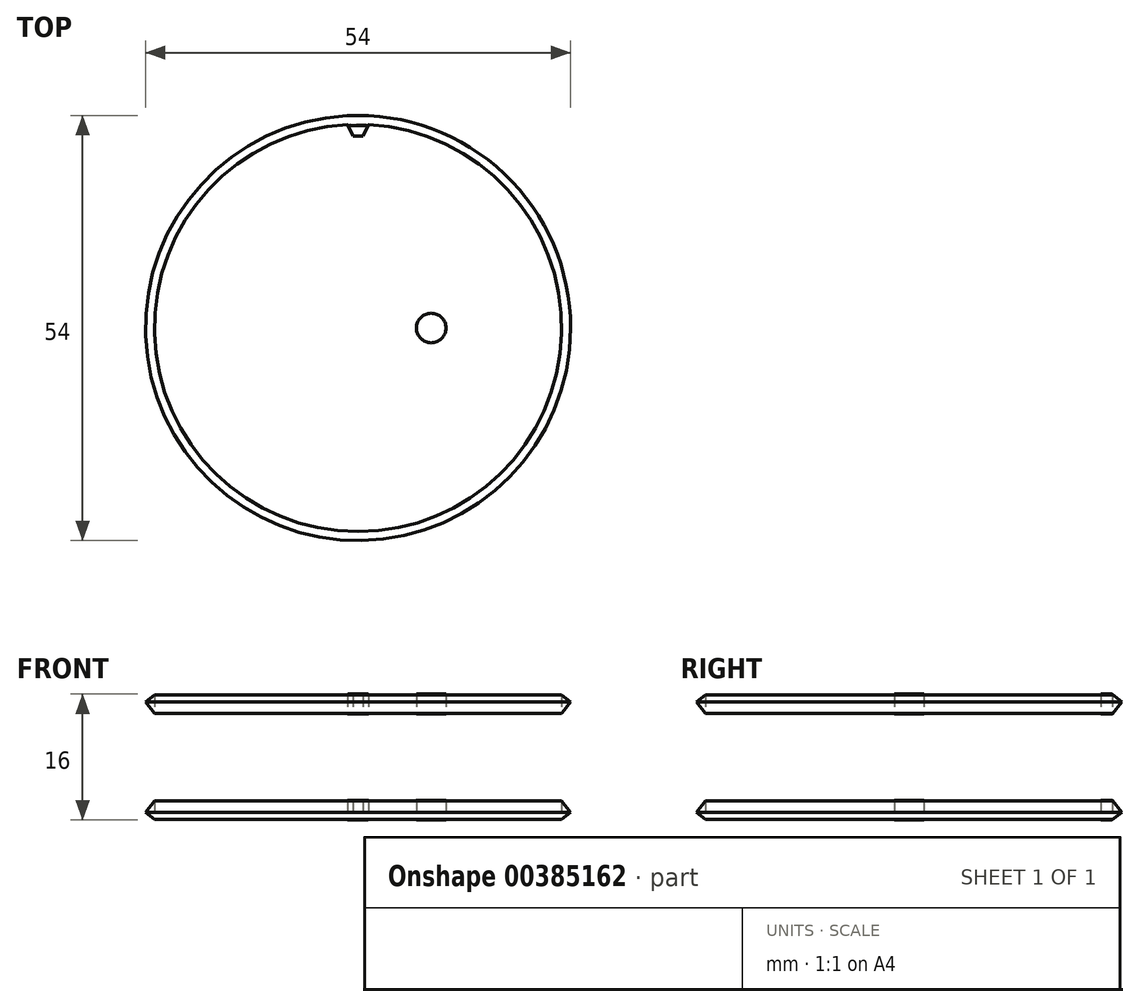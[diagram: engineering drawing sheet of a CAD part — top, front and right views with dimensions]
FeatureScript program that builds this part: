
annotation { "Feature Type Name" : "Feature", "Feature Type Description" : "" }
export const myFeature = defineFeature(function(context is Context, id is Id, definition is map)
    precondition{}
    {
        {
            var Q0;
            Q0=qCreatedBy(makeId("Top.planeOp"),FACE);
            var sketch = newSketch(context, id + "F0", { "sketchPlane" : qUnion([Q0])});
            skArc(sketch, "E0", {"start": v(-1.34, 25.84) * mm, "mid": v(0, -25.87) * mm, "end": v(1.34, 25.84) * mm});
            skCircle(sketch, "E1", {"center": v(0, 0) * mm, "radius": 24.37 * mm, "construction": true});
            skLineSegment(sketch, "E2", {"start": v(-0.65, 24.36) * mm, "end": v(-1.34, 25.84) * mm});
            skCircle(sketch, "E3", {"center": v(0, 0) * mm, "radius": 4.75 * mm});
            skArc(sketch, "E4", {"start": v(-0.65, 24.36) * mm, "mid": v(-0.33, 24.37) * mm, "end": v(0, 24.37) * mm});
            skLineSegment(sketch, "E5.MirrorCS", {"start": v(0.65, 24.36) * mm, "end": v(1.34, 25.84) * mm});
            skArc(sketch, "E6", {"start": v(-1.34, 25.84) * mm, "mid": v(0, 25.87) * mm, "end": v(1.34, 25.84) * mm});
            skArc(sketch, "E7.MirrorCS", {"start": v(0.65, 24.36) * mm, "mid": v(0.33, 24.37) * mm, "end": v(0, 24.37) * mm});
            skCircle(sketch, "E8", {"center": v(-9.3, 0) * mm, "radius": 1.88 * mm});
            skCircle(sketch, "E9.MirrorC", {"center": v(9.3, 0) * mm, "radius": 1.88 * mm});
            skSolve(sketch);
        }
        {
            var Q0;
            Q0=makeQuery(id+"F0.imprint","IMPRINT",FACE,{"disambiguationData":[TD([[makeQuery(id+"F0.imprint","IMPRINT",EDGE,{"derivedFrom":sQuery(id+"F0.wireOp",EDGE,"E0")}),1.0]])]});
            var Q1;
            Q1=makeQuery(id+"F0.imprint","IMPRINT",FACE,{"disambiguationData":[TD([[makeQuery(id+"F0.imprint","IMPRINT",EDGE,{"derivedFrom":sQuery(id+"F0.wireOp",EDGE,"E2")}),-1.0]])]});
            extrude(context, id + "F1", {"entities" : qUnion([Q0, Q1]), "depth" : 11 * mm, "offsetDistance" : 25 * mm});
        }
        {
            var Q0;
            Q0=makeQuery(id+"F0.imprint","IMPRINT",FACE,{"disambiguationData":[TD([[makeQuery(id+"F0.imprint","IMPRINT",EDGE,{"derivedFrom":sQuery(id+"F0.wireOp",EDGE,"E2")}),-1.0]])]});
            extrude(context, id + "F2", {"entities" : qUnion([Q0]), "operationType" : NewBodyOperationType.REMOVE, "endBound" : BoundingType.UP_TO_NEXT, "depth" : 25 * mm, "offsetDistance" : 25 * mm});
        }
        {
            var Q0;
            Q0=qCreatedBy(makeId("Right.planeOp"),FACE);
            var sketch = newSketch(context, id + "F3", { "sketchPlane" : qUnion([Q0])});
            skLineSegment(sketch, "E10", {"start": v(0, 27.65) * mm, "end": v(0, -39.13) * mm, "construction": true});
            skSolve(sketch);
        }
        {
            var Q0;
            Q0=qCreatedBy(makeId("Right.planeOp"),FACE);
            var sketch = newSketch(context, id + "F4", { "sketchPlane" : qUnion([Q0])});
            skLineSegment(sketch, "E11", {"start": v(0, 0) * mm, "end": v(0, -2.5) * mm});
            skLineSegment(sketch, "E12", {"start": v(0, -2.5) * mm, "end": v(25.73, -2.5) * mm});
            skLineSegment(sketch, "E13", {"start": v(27, -1.53) * mm, "end": v(25.84, 0) * mm});
            skLineSegment(sketch, "E14", {"start": v(25.84, 0) * mm, "end": v(0, 0) * mm});
            skLineSegment(sketch, "E15", {"start": v(27, -1.53) * mm, "end": v(25.73, -2.5) * mm});
            skPoint(sketch, "E16.0", {"position": v(25.84, 0) * mm});
            skPoint(sketch, "E17.0", {"position": v(25.84, 5.5) * mm});
            skLineSegment(sketch, "E18", {"start": v(25.84, 5.5) * mm, "end": v(32.61, 5.5) * mm, "construction": true});
            skLineSegment(sketch, "E19.MirrorCS", {"start": v(27, 12.53) * mm, "end": v(25.84, 11) * mm});
            skLineSegment(sketch, "E20.MirrorCS", {"start": v(27, 12.53) * mm, "end": v(25.73, 13.5) * mm});
            skLineSegment(sketch, "E21.MirrorCS", {"start": v(0, 13.5) * mm, "end": v(25.73, 13.5) * mm});
            skLineSegment(sketch, "E22.MirrorCS", {"start": v(0, 11) * mm, "end": v(0, 13.5) * mm});
            skLineSegment(sketch, "E23.MirrorCS", {"start": v(25.84, 11) * mm, "end": v(0, 11) * mm});
            skSolve(sketch);
        }
        {
            var Q0;
            Q0=makeQuery(id+"F4.imprint","IMPRINT",FACE,{"disambiguationData":[TD([[makeQuery(id+"F4.imprint","IMPRINT",EDGE,{"derivedFrom":sQuery(id+"F4.wireOp",EDGE,"E11")}),1.0]])]});
            var Q1;
            Q1=makeQuery(id+"F4.imprint","IMPRINT",FACE,{"disambiguationData":[TD([[makeQuery(id+"F4.imprint","IMPRINT",EDGE,{"derivedFrom":sQuery(id+"F4.wireOp",EDGE,"E19.MirrorCS")}),-1.0]])]});
            var Q2;
            Q2=sQuery(id+"F4.wireOp",EDGE,"E11");
            revolve(context, id + "F5", {"operationType" : NewBodyOperationType.ADD, "surfaceOperationType" : NewSurfaceOperationType.NEW, "entities" : qUnion([Q0, Q1]), "axis" : qUnion([Q2]), "revolveType" : RevolveType.FULL});
        }
        {
            var Q0;
            Q0=makeQuery(id+"F0.imprint","IMPRINT",FACE,{"disambiguationData":[TD([[makeQuery(id+"F0.imprint","IMPRINT",EDGE,{"derivedFrom":sQuery(id+"F0.wireOp",EDGE,"E8")}),1.0]])]});
            var Q1;
            Q1=makeQuery(id+"F0.imprint","IMPRINT",FACE,{"disambiguationData":[TD([[makeQuery(id+"F0.imprint","IMPRINT",EDGE,{"derivedFrom":sQuery(id+"F0.wireOp",EDGE,"E3")}),1.0]])]});
            var Q2;
            Q2=makeQuery(id+"F0.imprint","IMPRINT",FACE,{"disambiguationData":[TD([[makeQuery(id+"F0.imprint","IMPRINT",EDGE,{"derivedFrom":sQuery(id+"F0.wireOp",EDGE,"E9.MirrorC")}),-1.0]])]});
            extrude(context, id + "F6", {"entities" : qUnion([Q0, Q1, Q2]), "operationType" : NewBodyOperationType.REMOVE, "endBound" : BoundingType.THROUGH_ALL, "depth" : 25 * mm, "offsetDistance" : 25 * mm, "hasSecondDirection" : true, "secondDirectionBound" : BoundingType.THROUGH_ALL, "secondDirectionOppositeDirection" : true, "secondDirectionDepth" : 25 * mm});
        }
    });
